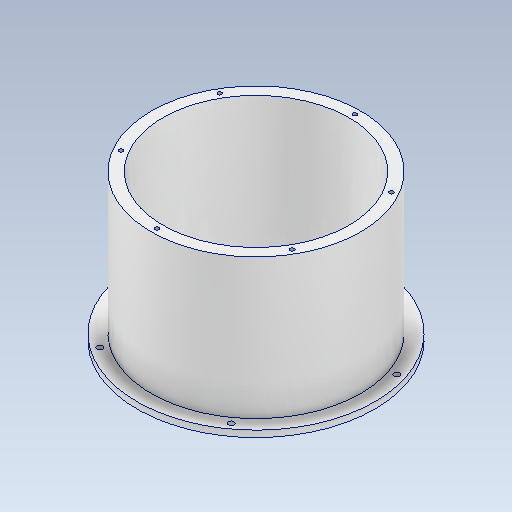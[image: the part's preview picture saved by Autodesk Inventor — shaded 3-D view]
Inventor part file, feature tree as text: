
AUTODESK INVENTOR PART (.ipt)
format: ipt  version: 2021 (Build 250183000, 183)  size: 189,952 bytes
history: native  units: mm
features: sketch x3, hole x2, projected_geometry x2, revolve x1, pattern_circular x1
ambient origin geometry x8: Origin, YZ Plane, XZ Plane, XY Plane, X Axis, Y Axis, Z Axis, Center Point
bodies: Body1 (feature_tree)
feature tree (9):
  revolve  "Revolution1"  [1 undecoded]
  hole  "Hole1"  [1 undecoded]
  pattern_circular  "Circular Pattern1"  Angle=90.0deg  [1 undecoded]
  hole  "Hole2"  [1 undecoded]
  sketch  "Sketch2"  dims[d4=5.0mm d5=11.0mm]
  sketch  "Sketch3"  dims[d6=9.0mm d8=110.0mm]
  projected_geometry  "Projected Loop1"
  sketch  "Sketch5"  dims[d9=4.0mm d10=90.0deg d11=5.5mm d12=5.5mm d13=4.5mm d14=7.0mm d15=9.4mm d16=2.0mm d17=90.0deg d18=8.0mm d19=20.594885mm d20=50.0mm d21=360.0deg d38=81.5mm d39=4.5mm d40=4.5mm d41=60.0mm d43=360.0deg d45=3.242mm d46=10.0mm d47=6.3mm d48=2.0mm d49=90.0deg d50=13.0mm d51=20.594885mm]
  projected_geometry  "Projected Loop3"
note: 4 required parameter values undecoded (feature->parameter linkage not recoverable at this tier; creation-order binding heuristic only, values carry confidence <= 0.55)